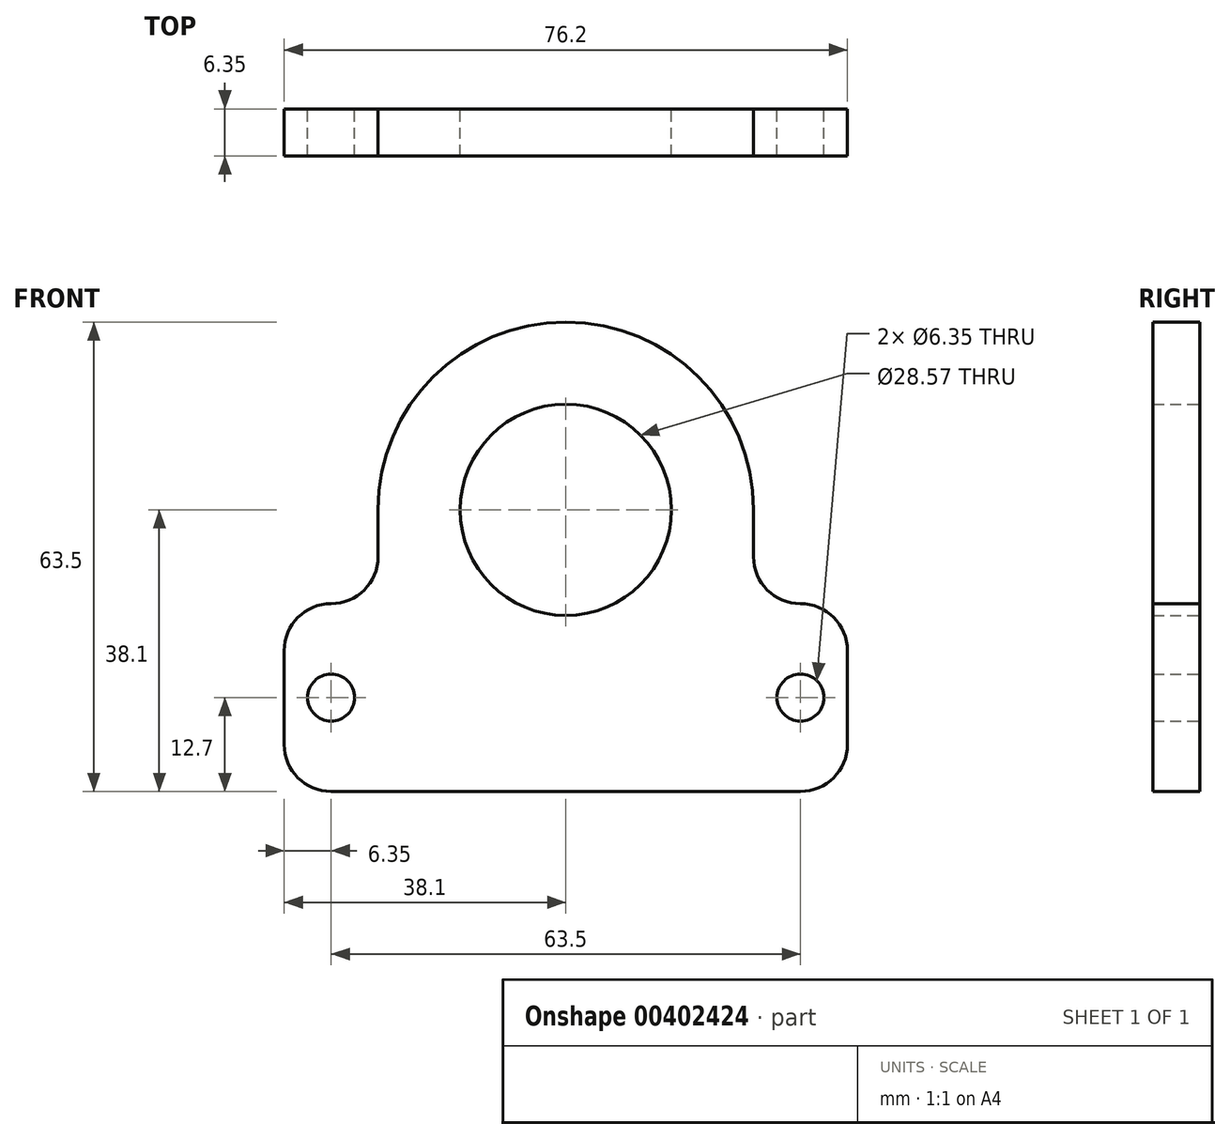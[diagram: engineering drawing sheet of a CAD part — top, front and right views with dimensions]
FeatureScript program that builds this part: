
annotation { "Feature Type Name" : "Feature", "Feature Type Description" : "" }
export const myFeature = defineFeature(function(context is Context, id is Id, definition is map)
    precondition{}
    {
        {
            var Q0;
            Q0=qCreatedBy(makeId("Front.planeOp"),FACE);
            var sketch = newSketch(context, id + "F0", { "sketchPlane" : qUnion([Q0])});
            skLineSegment(sketch, "E0.bottom", {"start": v(25.4, 0) * mm, "end": v(25.4, 0) * mm});
            skLineSegment(sketch, "E0.top", {"start": v(0, -63.5) * mm, "end": v(50.8, -63.5) * mm});
            skLineSegment(sketch, "E0.left", {"start": v(0, -25.4) * mm, "end": v(0, -31.75) * mm});
            skLineSegment(sketch, "E0.right", {"start": v(50.8, -25.4) * mm, "end": v(50.8, -31.75) * mm});
            skCircle(sketch, "E1", {"center": v(25.4, -25.4) * mm, "radius": 14.29 * mm});
            skCircle(sketch, "E2", {"center": v(-6.35, -50.8) * mm, "radius": 3.18 * mm});
            skCircle(sketch, "E3", {"center": v(57.15, -50.8) * mm, "radius": 3.18 * mm});
            skPoint(sketch, "E4.visualSharp", {"position": v(0, 0) * mm});
            skArc(sketch, "E4.filletArc", {"start": v(25.4, 0) * mm, "mid": v(7.44, -7.44) * mm, "end": v(0, -25.4) * mm});
            skPoint(sketch, "E5.visualSharp", {"position": v(50.8, 0) * mm});
            skArc(sketch, "E5.filletArc", {"start": v(50.8, -25.4) * mm, "mid": v(43.36, -7.44) * mm, "end": v(25.4, 0) * mm});
            skLineSegment(sketch, "E6.bottom", {"start": v(0, -63.5) * mm, "end": v(-6.35, -63.5) * mm});
            skLineSegment(sketch, "E6.top", {"start": v(-6.35, -38.1) * mm, "end": v(-6.35, -38.1) * mm});
            skLineSegment(sketch, "E6.left", {"start": v(0, -63.5) * mm, "end": v(0, -38.1) * mm});
            skLineSegment(sketch, "E6.right", {"start": v(-12.7, -57.15) * mm, "end": v(-12.7, -44.45) * mm});
            skLineSegment(sketch, "E7.bottom", {"start": v(50.8, -63.5) * mm, "end": v(57.15, -63.5) * mm});
            skLineSegment(sketch, "E7.top", {"start": v(57.15, -38.1) * mm, "end": v(57.15, -38.1) * mm});
            skLineSegment(sketch, "E7.left", {"start": v(50.8, -63.5) * mm, "end": v(50.8, -38.1) * mm});
            skLineSegment(sketch, "E7.right", {"start": v(63.5, -57.15) * mm, "end": v(63.5, -44.45) * mm});
            skPoint(sketch, "E8.visualSharp", {"position": v(-12.7, -38.1) * mm});
            skArc(sketch, "E8.filletArc", {"start": v(-6.35, -38.1) * mm, "mid": v(-10.84, -39.96) * mm, "end": v(-12.7, -44.45) * mm});
            skPoint(sketch, "E9.visualSharp", {"position": v(-12.7, -63.5) * mm});
            skArc(sketch, "E9.filletArc", {"start": v(-12.7, -57.15) * mm, "mid": v(-10.84, -61.64) * mm, "end": v(-6.35, -63.5) * mm});
            skPoint(sketch, "E10.visualSharp", {"position": v(63.5, -63.5) * mm});
            skArc(sketch, "E10.filletArc", {"start": v(57.15, -63.5) * mm, "mid": v(61.64, -61.64) * mm, "end": v(63.5, -57.15) * mm});
            skPoint(sketch, "E11.visualSharp", {"position": v(63.5, -38.1) * mm});
            skArc(sketch, "E11.filletArc", {"start": v(63.5, -44.45) * mm, "mid": v(61.64, -39.96) * mm, "end": v(57.15, -38.1) * mm});
            skArc(sketch, "E12.filletArc", {"start": v(-6.35, -38.1) * mm, "mid": v(-1.86, -36.24) * mm, "end": v(0, -31.75) * mm});
            skPoint(sketch, "E13.newPointA", {"position": v(50.8, -63.5) * mm});
            skArc(sketch, "E13.filletArc", {"start": v(50.8, -31.75) * mm, "mid": v(52.66, -36.24) * mm, "end": v(57.15, -38.1) * mm});
            skSolve(sketch);
        }
        {
            var Q0;
            Q0 = qSketchRegion(id + "F0", true);
            extrude(context, id + "F1", {"entities" : qUnion([Q0]), "depth" : 6.35 * mm});
        }
    });
